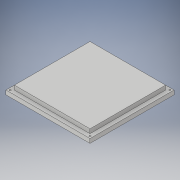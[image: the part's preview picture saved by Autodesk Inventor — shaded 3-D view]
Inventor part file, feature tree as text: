
AUTODESK INVENTOR PART (.ipt)
format: ipt  version: 2017 (Build 210142000, 142)  size: 130,048 bytes
history: native  units: in
note: dims shown in document units (in); Inventor stores cm internally (conversion verified against a paired STEP export)
features: sketch x4, hole x4, extrude x2
ambient origin geometry x8: Origin, YZ Plane, XZ Plane, XY Plane, X Axis, Y Axis, Z Axis, Center Point
bodies: Solid1 (feature_tree)
feature tree (10):
  sketch  "Sketch1"  dims[d0=3.937in d1=3.937in]
  extrude  "Extrusion1"  Depth=3.937in
  sketch  "Sketch3"  dims[d6=0.0984in d7=0.0984in]
  hole  "Hole1"  [1 undecoded]
  hole  "Hole2"  [1 undecoded]
  hole  "Hole3"  [1 undecoded]
  hole  "Hole4"  [1 undecoded]
  extrude  "Extrusion2"  Depth=0.1969in
  sketch  "Sketch2"  dims[d3=1.9685in d4=0.1969in d5=0.0in]
  sketch  "Sketch4"  dims[d8=0.0787in d9=0.0984in d10=0.0984in d11=0.0984in d12=0.0984in d13=0.0984in d14=0.0984in d15=0.3937in d16=0.3937in d17=0.0787in d18=0.2953in d19=0.1476in d20=0.0984in d21=90.0deg d22=0.3937in d23=0.8108in d24=0.3937in d25=0.3937in d26=0.0787in d27=0.2953in d28=0.1476in d29=0.0984in d30=90.0deg d31=0.3937in d32=0.8108in d33=0.3937in d34=0.3937in d35=0.0787in d36=0.2953in d37=0.1476in d38=0.0984in d39=90.0deg d40=0.3937in d41=0.8108in d42=0.0787in d43=0.2953in d44=0.1476in d45=0.0984in d46=90.0deg d47=0.3937in d48=0.8108in d49=0.1969in d50=0.1969in d51=0.1969in d52=0.1969in d53=0.1969in d54=0.0in]
note: 4 required parameter values undecoded (feature->parameter linkage not recoverable at this tier; creation-order binding heuristic only, values carry confidence <= 0.55)
